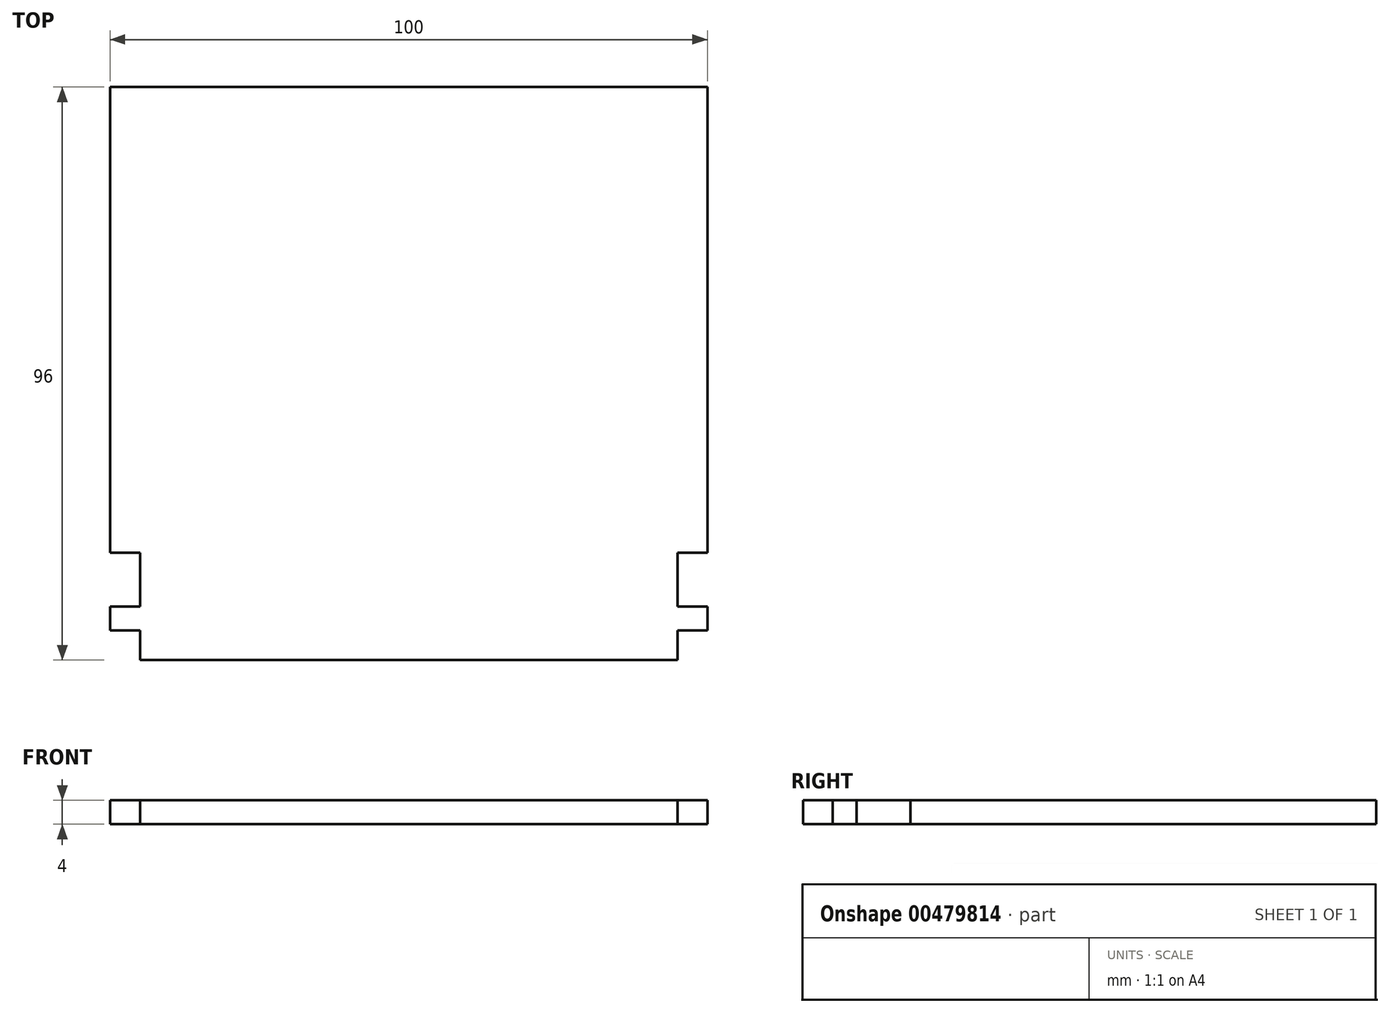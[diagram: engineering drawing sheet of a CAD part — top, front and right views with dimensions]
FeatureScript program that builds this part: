
annotation { "Feature Type Name" : "Feature", "Feature Type Description" : "" }
export const myFeature = defineFeature(function(context is Context, id is Id, definition is map)
    precondition{}
    {
        {
            var Q0;
            Q0=qCreatedBy(makeId("Top.planeOp"),FACE);
            var sketch = newSketch(context, id + "F0", { "sketchPlane" : qUnion([Q0])});
            skLineSegment(sketch, "E0.bottom", {"start": v(0, 0) * mm, "end": v(100, 0) * mm});
            skLineSegment(sketch, "E0.top", {"start": v(0, 100) * mm, "end": v(100, 100) * mm});
            skLineSegment(sketch, "E0.left", {"start": v(0, 0) * mm, "end": v(0, 100) * mm});
            skLineSegment(sketch, "E0.right", {"start": v(100, 0) * mm, "end": v(100, 100) * mm});
            skSolve(sketch);
        }
        {
            var Q0;
            Q0 = qSketchRegion(id + "F0", true);
            extrude(context, id + "F1", {"entities" : qUnion([Q0]), "depth" : 4 * mm});
        }
        {
            var Q0;
            Q0=qCreatedBy(makeId("Top.planeOp"),FACE);
            var sketch = newSketch(context, id + "F2", { "sketchPlane" : qUnion([Q0])});
            skLineSegment(sketch, "E1.bottom", {"start": v(0, 0) * mm, "end": v(5, 0) * mm});
            skLineSegment(sketch, "E1.top", {"start": v(0, 22) * mm, "end": v(5, 22) * mm});
            skLineSegment(sketch, "E1.left", {"start": v(0, 0) * mm, "end": v(0, 22) * mm});
            skLineSegment(sketch, "E1.right", {"start": v(5, 0) * mm, "end": v(5, 22) * mm});
            skLineSegment(sketch, "E2.bottom", {"start": v(100, 0) * mm, "end": v(95, 0) * mm});
            skLineSegment(sketch, "E2.top", {"start": v(100, 22) * mm, "end": v(95, 22) * mm});
            skLineSegment(sketch, "E2.left", {"start": v(100, 0) * mm, "end": v(100, 22) * mm});
            skLineSegment(sketch, "E2.right", {"start": v(95, 0) * mm, "end": v(95, 22) * mm});
            skSolve(sketch);
        }
        {
            var Q0;
            Q0 = qSketchRegion(id + "F2", true);
            extrude(context, id + "F3", {"entities" : qUnion([Q0]), "operationType" : NewBodyOperationType.REMOVE, "depth" : 4 * mm});
        }
        {
            var Q0;
            Q0=qCreatedBy(makeId("Top.planeOp"),FACE);
            var sketch = newSketch(context, id + "F4", { "sketchPlane" : qUnion([Q0])});
            skLineSegment(sketch, "E3.bottom", {"start": v(5, 13) * mm, "end": v(-5, 13) * mm});
            skLineSegment(sketch, "E3.top", {"start": v(5, 9) * mm, "end": v(-5, 9) * mm});
            skLineSegment(sketch, "E3.left", {"start": v(5, 13) * mm, "end": v(5, 9) * mm});
            skLineSegment(sketch, "E3.right", {"start": v(-5, 13) * mm, "end": v(-5, 9) * mm});
            skLineSegment(sketch, "E4.bottom", {"start": v(95, 13) * mm, "end": v(105, 13) * mm});
            skLineSegment(sketch, "E4.top", {"start": v(95, 9) * mm, "end": v(105, 9) * mm});
            skLineSegment(sketch, "E4.left", {"start": v(95, 13) * mm, "end": v(95, 9) * mm});
            skLineSegment(sketch, "E4.right", {"start": v(105, 13) * mm, "end": v(105, 9) * mm});
            skSolve(sketch);
        }
        {
            var Q0;
            Q0 = qSketchRegion(id + "F4", true);
            extrude(context, id + "F5", {"entities" : qUnion([Q0]), "operationType" : NewBodyOperationType.ADD, "depth" : 4 * mm});
        }
        {
            var Q0;
            Q0=qCreatedBy(makeId("Top.planeOp"),FACE);
            var sketch = newSketch(context, id + "F6", { "sketchPlane" : qUnion([Q0])});
            skLineSegment(sketch, "E5.bottom", {"start": v(-5, 13) * mm, "end": v(0, 13) * mm});
            skLineSegment(sketch, "E5.top", {"start": v(-5, 9) * mm, "end": v(0, 9) * mm});
            skLineSegment(sketch, "E5.left", {"start": v(-5, 13) * mm, "end": v(-5, 9) * mm});
            skLineSegment(sketch, "E5.right", {"start": v(0, 13) * mm, "end": v(0, 9) * mm});
            skSolve(sketch);
        }
        {
            var Q0;
            Q0 = qSketchRegion(id + "F6", true);
            extrude(context, id + "F7", {"entities" : qUnion([Q0]), "operationType" : NewBodyOperationType.REMOVE, "depth" : 4 * mm, "offsetDistance" : 25 * mm});
        }
        {
            var Q0;
            Q0=qCreatedBy(makeId("Top.planeOp"),FACE);
            var sketch = newSketch(context, id + "F8", { "sketchPlane" : qUnion([Q0])});
            skLineSegment(sketch, "E6.bottom", {"start": v(105, 9) * mm, "end": v(100, 9) * mm});
            skLineSegment(sketch, "E6.top", {"start": v(105, 13) * mm, "end": v(100, 13) * mm});
            skLineSegment(sketch, "E6.left", {"start": v(105, 9) * mm, "end": v(105, 13) * mm});
            skLineSegment(sketch, "E6.right", {"start": v(100, 9) * mm, "end": v(100, 13) * mm});
            skSolve(sketch);
        }
        {
            var Q0;
            Q0 = qSketchRegion(id + "F8", true);
            extrude(context, id + "F9", {"entities" : qUnion([Q0]), "operationType" : NewBodyOperationType.REMOVE, "depth" : 4 * mm, "offsetDistance" : 25 * mm});
        }
        {
            var Q0;
            Q0=qCreatedBy(makeId("Top.planeOp"),FACE);
            var sketch = newSketch(context, id + "F10", { "sketchPlane" : qUnion([Q0])});
            skLineSegment(sketch, "E7.bottom", {"start": v(95, 0) * mm, "end": v(5, 0) * mm});
            skLineSegment(sketch, "E7.top", {"start": v(95, 4) * mm, "end": v(5, 4) * mm});
            skLineSegment(sketch, "E7.left", {"start": v(95, 0) * mm, "end": v(95, 4) * mm});
            skLineSegment(sketch, "E7.right", {"start": v(5, 0) * mm, "end": v(5, 4) * mm});
            skSolve(sketch);
        }
        {
            var Q0;
            Q0 = qSketchRegion(id + "F10", true);
            extrude(context, id + "F11", {"entities" : qUnion([Q0]), "operationType" : NewBodyOperationType.REMOVE, "depth" : 4 * mm, "offsetDistance" : 25 * mm});
        }
    });
